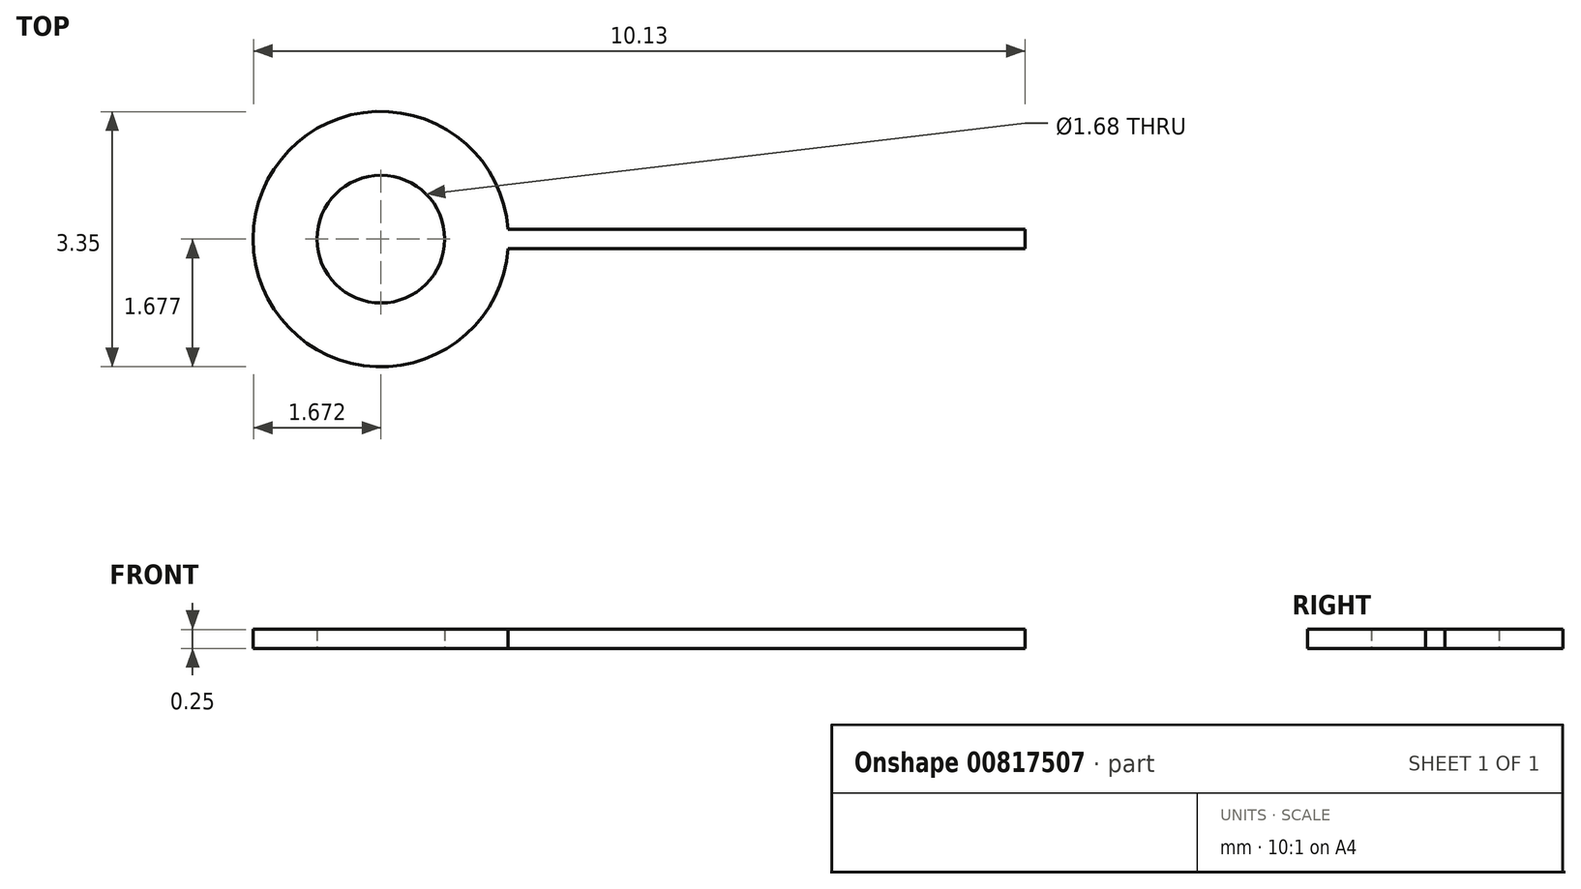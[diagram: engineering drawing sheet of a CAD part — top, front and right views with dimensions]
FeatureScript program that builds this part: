
annotation { "Feature Type Name" : "Feature", "Feature Type Description" : "" }
export const myFeature = defineFeature(function(context is Context, id is Id, definition is map)
    precondition{}
    {
        {
            var Q0;
            Q0=qCreatedBy(makeId("Top.planeOp"),FACE);
            var sketch = newSketch(context, id + "F0", { "sketchPlane" : qUnion([Q0])});
            skLineSegment(sketch, "E0.bottom", {"start": v(0, 0) * mm, "end": v(7.62, 0) * mm});
            skLineSegment(sketch, "E0.top", {"start": v(0, 0.25) * mm, "end": v(7.62, 0.25) * mm});
            skLineSegment(sketch, "E0.right", {"start": v(7.62, 0) * mm, "end": v(7.62, 0.25) * mm});
            skLineSegment(sketch, "E1", {"start": v(0, 0) * mm, "end": v(0, 0.25) * mm});
            skLineSegment(sketch, "E2", {"start": v(0, 0.13) * mm, "end": v(-0.84, 0.13) * mm});
            skLineSegment(sketch, "E3", {"start": v(0, 0.13) * mm, "end": v(0.84, 0.13) * mm});
            skCircle(sketch, "E4", {"center": v(-0.84, 0.13) * mm, "radius": 1.68 * mm});
            skCircle(sketch, "E5", {"center": v(-0.84, 0.13) * mm, "radius": 0.84 * mm});
            skSolve(sketch);
        }
        {
            var Q0;
            Q0=qSketchRegion(id+"F0",true);
            extrude(context, id + "F1", {"entities" : qUnion([Q0]), "depth" : 0.25 * mm, "offsetDistance" : 25.4 * mm});
        }
    });
